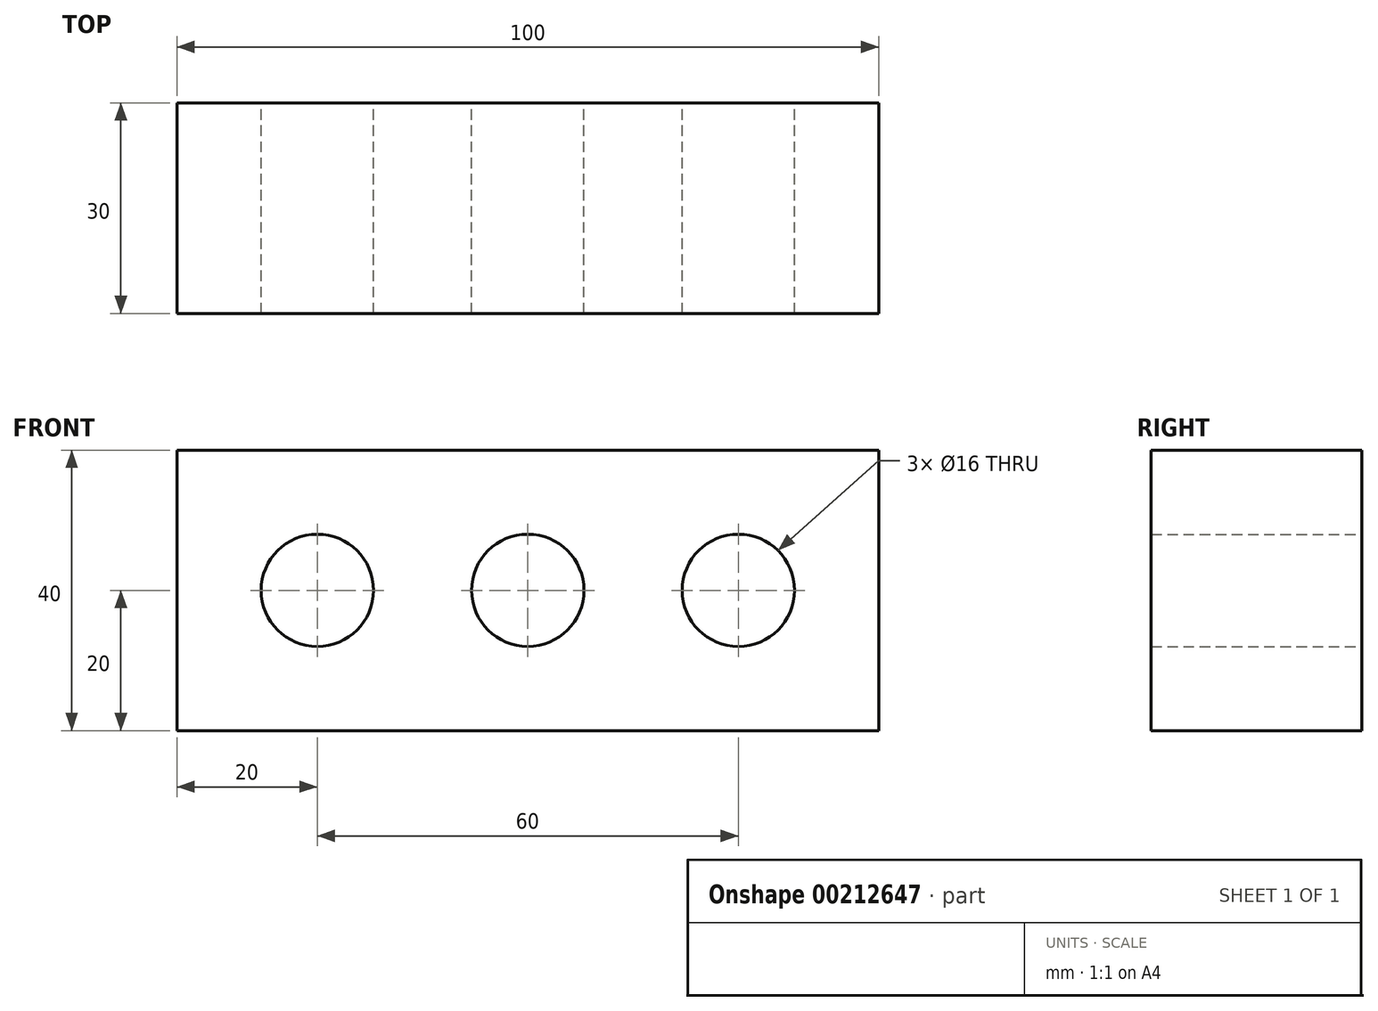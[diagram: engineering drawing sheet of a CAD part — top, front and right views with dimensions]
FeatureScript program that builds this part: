
annotation { "Feature Type Name" : "Feature", "Feature Type Description" : "" }
export const myFeature = defineFeature(function(context is Context, id is Id, definition is map)
    precondition{}
    {
        {
            var Q0;
            Q0=qCreatedBy(makeId("Front.planeOp"),FACE);
            var sketch = newSketch(context, id + "F0", { "sketchPlane" : qUnion([Q0])});
            skLineSegment(sketch, "E0.bottom", {"start": v(-50, 20) * mm, "end": v(50, 20) * mm});
            skLineSegment(sketch, "E0.top", {"start": v(-50, -20) * mm, "end": v(50, -20) * mm});
            skLineSegment(sketch, "E0.left", {"start": v(-50, 20) * mm, "end": v(-50, -20) * mm});
            skLineSegment(sketch, "E0.right", {"start": v(50, 20) * mm, "end": v(50, -20) * mm});
            skCircle(sketch, "E1", {"center": v(0, 0) * mm, "radius": 8 * mm});
            skCircle(sketch, "E2", {"center": v(30, 0) * mm, "radius": 8 * mm});
            skCircle(sketch, "E3", {"center": v(-30, 0) * mm, "radius": 8 * mm});
            skSolve(sketch);
        }
        {
            var Q0;
            Q0 = qSketchRegion(id + "F0", true);
            extrude(context, id + "F1", {"entities" : qUnion([Q0]), "depth" : 30 * mm});
        }
    });
